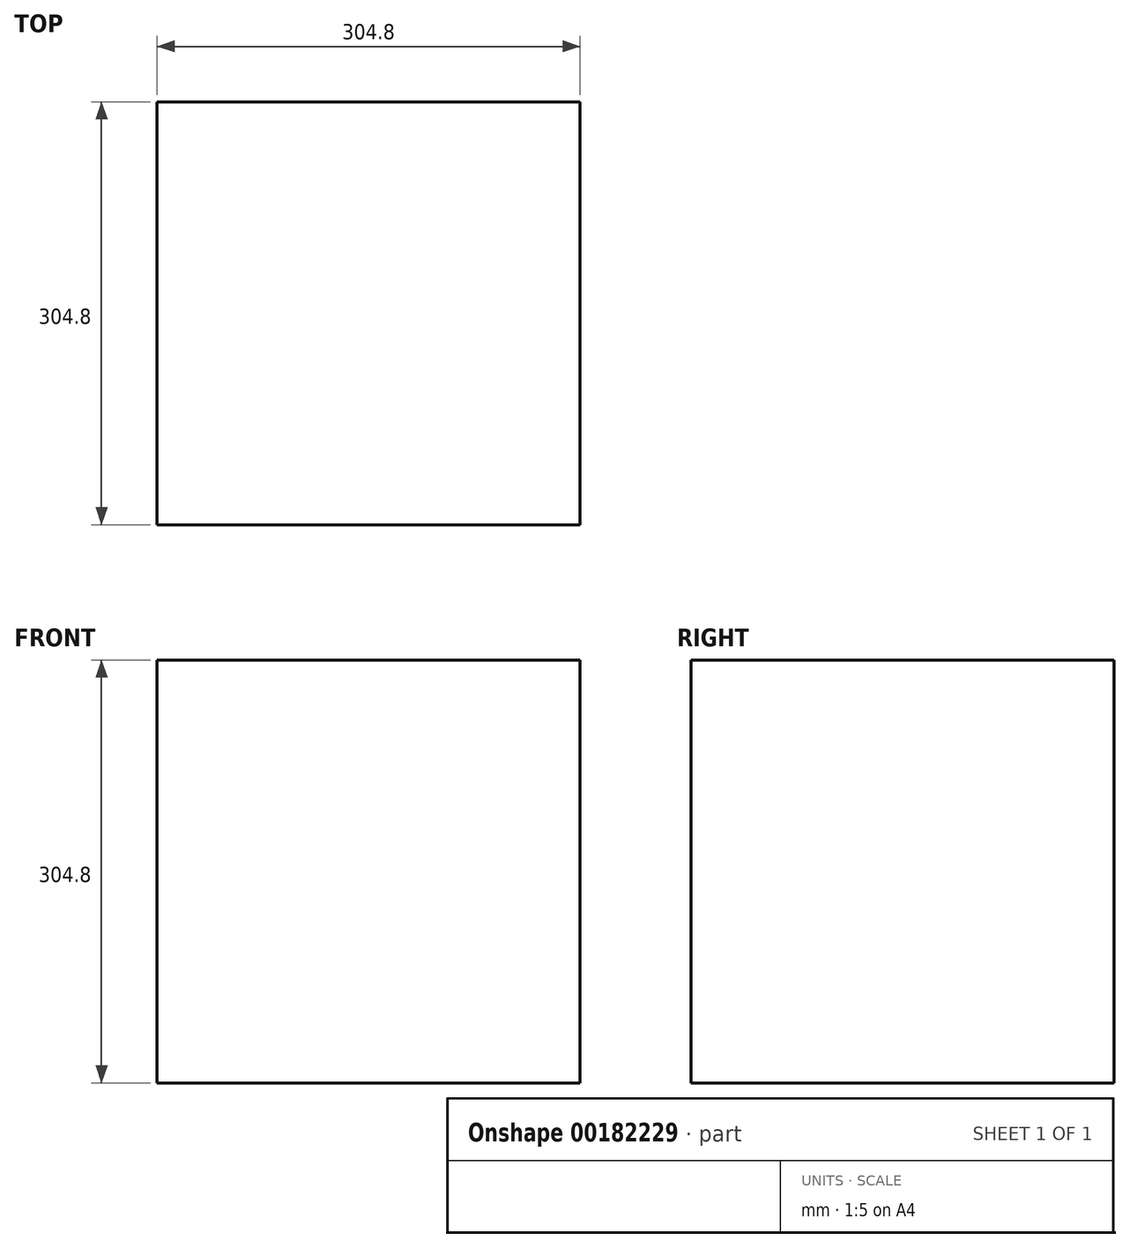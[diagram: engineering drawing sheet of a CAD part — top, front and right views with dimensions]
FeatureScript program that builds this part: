
annotation { "Feature Type Name" : "Feature", "Feature Type Description" : "" }
export const myFeature = defineFeature(function(context is Context, id is Id, definition is map)
    precondition{}
    {
        {
            var Q0;
            Q0=qCreatedBy(makeId("Front.planeOp"),FACE);
            var sketch = newSketch(context, id + "F0", { "sketchPlane" : qUnion([Q0])});
            skLineSegment(sketch, "E0.bottom", {"start": v(0, 304.8) * mm, "end": v(304.8, 304.8) * mm});
            skLineSegment(sketch, "E0.top", {"start": v(0, 0) * mm, "end": v(304.8, 0) * mm});
            skLineSegment(sketch, "E0.left", {"start": v(0, 304.8) * mm, "end": v(0, 0) * mm});
            skLineSegment(sketch, "E0.right", {"start": v(304.8, 304.8) * mm, "end": v(304.8, 0) * mm});
            skSolve(sketch);
        }
        {
            var Q0;
            Q0=qSketchRegion(id+"F0",true);
            extrude(context, id + "F1", {"entities" : qUnion([Q0]), "oppositeDirection" : true, "depth" : 304.8 * mm});
        }
    });
